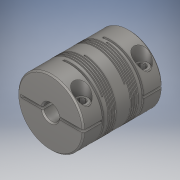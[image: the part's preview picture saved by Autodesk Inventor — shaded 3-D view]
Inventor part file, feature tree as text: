
AUTODESK INVENTOR PART (.ipt)
format: ipt  version: 2017 (Build 210142000, 142)  size: 2,531,840 bytes
history: native  units: in
note: dims shown in document units (in); Inventor stores cm internally (conversion verified against a paired STEP export)
features: boolean_combine x2, other x1, mirror x1
ambient origin geometry x8: Origin, YZ Plane, XZ Plane, XY Plane, X Axis, Y Axis, Z Axis, Center Point
bodies: Solid1 (feature_tree), Solid2 (feature_tree), Solid3 (feature_tree)
feature tree (4):
  other  "2464K300_ALUMINUM HELICAL FLEXIBLE SHAFT COUPLING.STEP"
  boolean_combine  "Combine3"
  mirror  "Mirror1[2]"
  boolean_combine  "Combine4"
